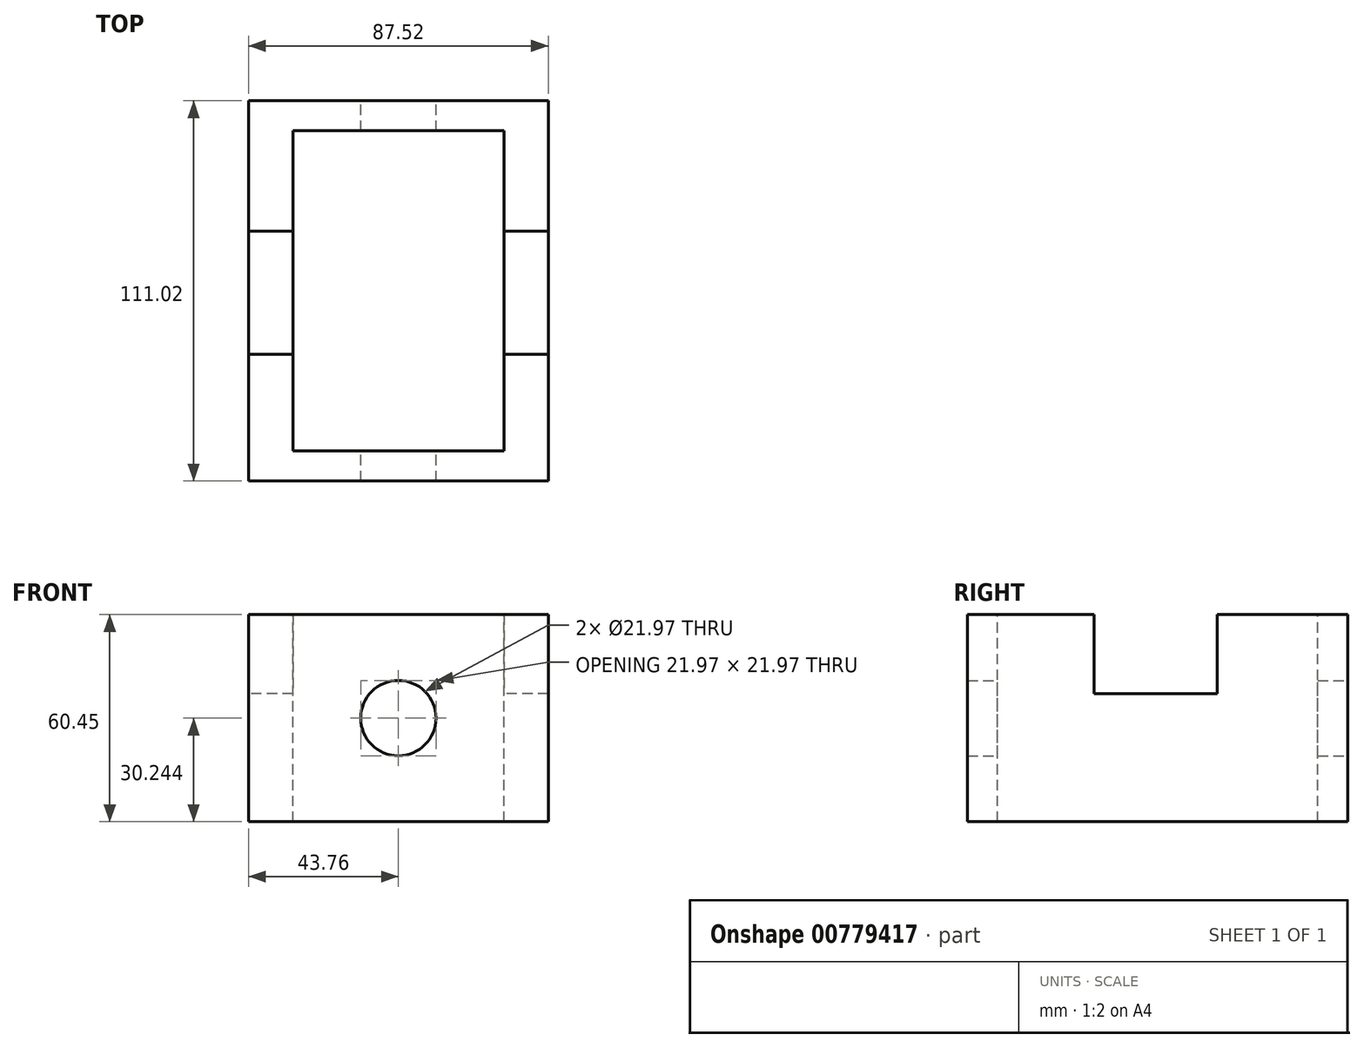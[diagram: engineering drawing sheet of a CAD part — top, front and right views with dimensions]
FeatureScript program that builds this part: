
annotation { "Feature Type Name" : "Feature", "Feature Type Description" : "" }
export const myFeature = defineFeature(function(context is Context, id is Id, definition is map)
    precondition{}
    {
        {
            var Q0;
            Q0=qCreatedBy(makeId("Top.planeOp"),FACE);
            var sketch = newSketch(context, id + "F0", { "sketchPlane" : qUnion([Q0])});
            skLineSegment(sketch, "E0.bottom", {"start": v(-43.76, 55.51) * mm, "end": v(43.76, 55.51) * mm});
            skLineSegment(sketch, "E0.top", {"start": v(-43.76, -55.51) * mm, "end": v(43.76, -55.51) * mm});
            skLineSegment(sketch, "E0.left", {"start": v(-43.76, 55.51) * mm, "end": v(-43.76, -55.51) * mm});
            skLineSegment(sketch, "E0.right", {"start": v(43.76, 55.51) * mm, "end": v(43.76, -55.51) * mm});
            skPoint(sketch, "E0.middle", {"position": v(0, 0) * mm});
            skSolve(sketch);
        }
        {
            var Q0;
            Q0=makeQuery(id+"F0.imprint","IMPRINT",FACE,{"disambiguationData":[TD([[makeQuery(id+"F0.imprint","IMPRINT",EDGE,{"derivedFrom":sQuery(id+"F0.wireOp",EDGE,"E0.bottom")}),-1.0]])]});
            extrude(context, id + "F1", {"entities" : qUnion([Q0]), "depth" : 60.45 * mm, "offsetDistance" : 25.4 * mm});
        }
        {
            var Q0;
            Q0=makeQuery(id+"F1.opExtrude","CAP_FACE",FACE,{"disambiguationData":[OSD([sQuery(id+"F0.wireOp",EDGE,"E0.bottom"),sQuery(id+"F0.wireOp",EDGE,"E0.top"),sQuery(id+"F0.wireOp",EDGE,"E0.left"),sQuery(id+"F0.wireOp",EDGE,"E0.right")])],"isStart":false});
            var sketch = newSketch(context, id + "F2", { "sketchPlane" : qUnion([Q0])});
            skLineSegment(sketch, "E1.bottom", {"start": v(-30.78, 46.74) * mm, "end": v(30.78, 46.74) * mm});
            skLineSegment(sketch, "E1.top", {"start": v(-30.78, -46.74) * mm, "end": v(30.78, -46.74) * mm});
            skLineSegment(sketch, "E1.left", {"start": v(-30.78, 46.74) * mm, "end": v(-30.78, -46.74) * mm});
            skLineSegment(sketch, "E1.right", {"start": v(30.78, 46.74) * mm, "end": v(30.78, -46.74) * mm});
            skPoint(sketch, "E1.middle", {"position": v(0, 0) * mm});
            skSolve(sketch);
        }
        {
            var Q0;
            Q0=makeQuery(id+"F2.imprint","IMPRINT",FACE,{"disambiguationData":[TD([[makeQuery(id+"F2.imprint","IMPRINT",EDGE,{"derivedFrom":sQuery(id+"F2.wireOp",EDGE,"E1.bottom")}),-1.0]])]});
            extrude(context, id + "F3", {"entities" : qUnion([Q0]), "operationType" : NewBodyOperationType.REMOVE, "oppositeDirection" : true, "depth" : 25.4 * mm, "offsetDistance" : 25.4 * mm});
        }
        {
            var Q0;
            Q0=makeQuery(id+"F3.boolean.opBoolean","COPY",FACE,{"derivedFrom":makeQuery(id+"F3.opExtrude","CAP_FACE",FACE,{"disambiguationData":[OSD([sQuery(id+"F2.wireOp",EDGE,"E1.bottom"),sQuery(id+"F2.wireOp",EDGE,"E1.top"),sQuery(id+"F2.wireOp",EDGE,"E1.left"),sQuery(id+"F2.wireOp",EDGE,"E1.right")])],"isStart":false})});
            extrude(context, id + "F4", {"entities" : qUnion([Q0]), "operationType" : NewBodyOperationType.REMOVE, "oppositeDirection" : true, "depth" : 25.4 * mm, "offsetDistance" : 25.4 * mm});
        }
        {
            var Q0;
            Q0=makeQuery(id+"F4.boolean.opBoolean","COPY",FACE,{"derivedFrom":makeQuery(id+"F4.opExtrude","CAP_FACE",FACE,{"disambiguationData":[OSD([sQuery(id+"F2.wireOp",EDGE,"E1.bottom"),sQuery(id+"F2.wireOp",EDGE,"E1.top"),sQuery(id+"F2.wireOp",EDGE,"E1.left"),sQuery(id+"F2.wireOp",EDGE,"E1.right")])],"isStart":false})});
            extrude(context, id + "F5", {"entities" : qUnion([Q0]), "operationType" : NewBodyOperationType.REMOVE, "oppositeDirection" : true, "depth" : 25.4 * mm, "offsetDistance" : 25.4 * mm});
        }
        {
            var Q0;
            Q0=makeQuery(id+"F1.opExtrude","SWEPT_FACE",FACE,{"disambiguationData":[OSD([sQuery(id+"F0.wireOp",EDGE,"E0.bottom")])]});
            var sketch = newSketch(context, id + "F6", { "sketchPlane" : qUnion([Q0])});
            skCircle(sketch, "E2", {"center": v(0, 30.24) * mm, "radius": 10.98 * mm});
            skSolve(sketch);
        }
        {
            var Q0;
            Q0=makeQuery(id+"F6.imprint","IMPRINT",FACE,{"disambiguationData":[TD([[makeQuery(id+"F6.imprint","IMPRINT",EDGE,{"derivedFrom":sQuery(id+"F6.wireOp",EDGE,"E2")}),1.0]])]});
            extrude(context, id + "F7", {"entities" : qUnion([Q0]), "operationType" : NewBodyOperationType.REMOVE, "endBound" : BoundingType.THROUGH_ALL, "oppositeDirection" : true, "depth" : 25.4 * mm, "offsetDistance" : 25.4 * mm});
        }
        {
            var Q0;
            Q0=makeQuery(id+"F1.opExtrude","SWEPT_FACE",FACE,{"disambiguationData":[OSD([sQuery(id+"F0.wireOp",EDGE,"E0.left")])]});
            var sketch = newSketch(context, id + "F8", { "sketchPlane" : qUnion([Q0])});
            skLineSegment(sketch, "E3.bottom", {"start": v(-17.42, 60.45) * mm, "end": v(18.55, 60.45) * mm});
            skLineSegment(sketch, "E3.top", {"start": v(-17.42, 37.39) * mm, "end": v(18.55, 37.39) * mm});
            skLineSegment(sketch, "E3.left", {"start": v(-17.42, 60.45) * mm, "end": v(-17.42, 37.39) * mm});
            skLineSegment(sketch, "E3.right", {"start": v(18.55, 60.45) * mm, "end": v(18.55, 37.39) * mm});
            skSolve(sketch);
        }
        {
            var Q0;
            Q0 = qSketchRegion(id + "F8", true);
            extrude(context, id + "F9", {"entities" : qUnion([Q0]), "operationType" : NewBodyOperationType.REMOVE, "endBound" : BoundingType.THROUGH_ALL, "oppositeDirection" : true, "depth" : 25.4 * mm, "offsetDistance" : 25.4 * mm});
        }
    });
